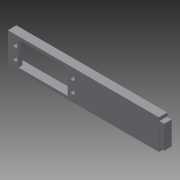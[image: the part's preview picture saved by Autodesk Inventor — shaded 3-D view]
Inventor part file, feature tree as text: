
AUTODESK INVENTOR PART (.ipt)
format: ipt  version: 2015 SP2 (Build 190223200, 223)  size: 148,480 bytes
history: native  units: mm
features: sketch x7, extrude x5, hole x1
ambient origin geometry x8: Origin, YZ Plane, XZ Plane, XY Plane, X Axis, Y Axis, Z Axis, Center Point
bodies: Solid1 (feature_tree)
feature tree (13):
  extrude  "Extrusion1"  Depth=60.0mm
  hole  "Hole1"  [1 undecoded]
  extrude  "Extrusion2"  Depth=4.0mm
  sketch  "Sketch9"  dims[d12=3.0mm d13=3.0mm]
  extrude  "Extrusion3"  Depth=3.0mm
  extrude  "Extrusion4"  Depth=3.0mm
  extrude  "Extrusion5"  Depth=3.0mm
  sketch  "Sketch2"  dims[d2=25.0mm d3=60.0mm]
  sketch  "Sketch4"  dims[d4=3.0mm d5=0.0mm d8=4.0mm]
  sketch  "Sketch8"  dims[d9=4.0mm d11=40.23mm]
  sketch  "Sketch10"  dims[d14=3.0mm d15=3.0mm]
  sketch  "Sketch11"  dims[d16=4.0mm d17=6.0mm d18=4.0mm d19=2.0mm d20=90.0deg d21=8.0mm d22=20.594885mm d23=3.0mm]
  sketch  "Sketch12"  dims[d24=3.0mm d25=3.0mm d26=3.0mm d27=20.0mm d28=3.0mm d29=0.0mm d30=41.0mm d35=4.0mm d36=3.0mm d37=0.0mm d38=0.0mm d39=66.0mm d40=7.0mm d41=0.0mm d42=19.5mm d43=6.115mm d44=4.0mm d45=0.0mm]
note: 1 required parameter value undecoded (feature->parameter linkage not recoverable at this tier; creation-order binding heuristic only, values carry confidence <= 0.55)
